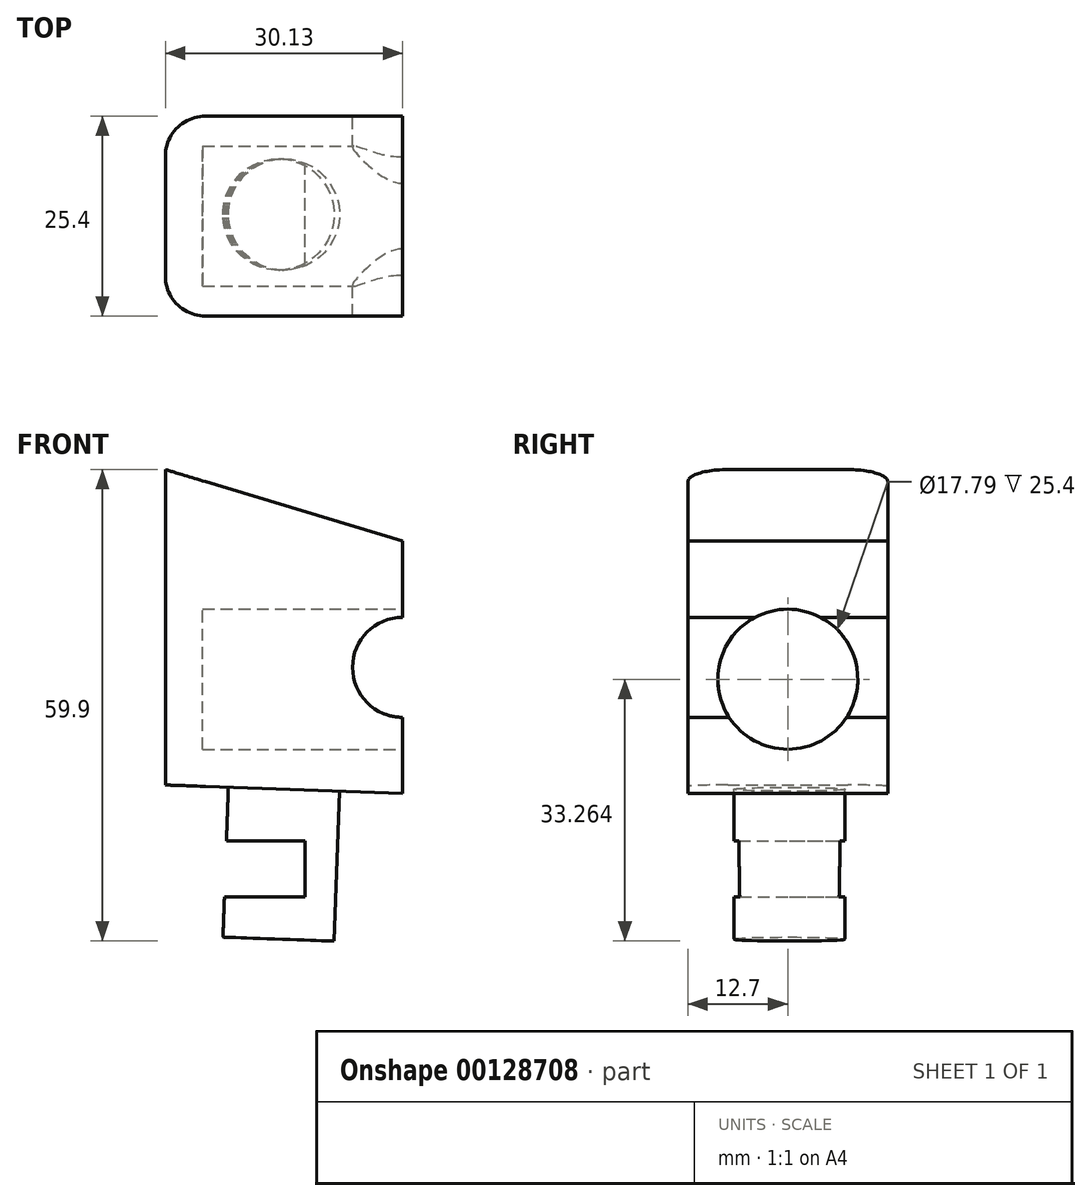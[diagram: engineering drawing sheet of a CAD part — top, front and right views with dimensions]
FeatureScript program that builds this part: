
annotation { "Feature Type Name" : "Feature", "Feature Type Description" : "" }
export const myFeature = defineFeature(function(context is Context, id is Id, definition is map)
    precondition{}
    {
        {
            var Q0;
            Q0=qCreatedBy(makeId("Front.planeOp"),FACE);
            var sketch = newSketch(context, id + "F0", { "sketchPlane" : qUnion([Q0])});
            skLineSegment(sketch, "E0", {"start": v(-39, 50.96) * mm, "end": v(-8.87, 41.86) * mm});
            skLineSegment(sketch, "E1", {"start": v(-8.87, 41.86) * mm, "end": v(-8.87, 9.8) * mm});
            skLineSegment(sketch, "E2", {"start": v(-39, 50.96) * mm, "end": v(-39, 10.89) * mm});
            skLineSegment(sketch, "E3", {"start": v(-39, 10.89) * mm, "end": v(-8.87, 9.8) * mm});
            skSolve(sketch);
        }
        {
            var Q0;
            Q0 = qSketchRegion(id + "F0", true);
            extrude(context, id + "F1", {"entities" : qUnion([Q0]), "depth" : 25.4 * mm});
        }
        {
            var Q0;
            Q0=makeQuery(id+"F1.opExtrude","SWEPT_FACE",FACE,{"disambiguationData":[OSD([sQuery(id+"F0.wireOp",EDGE,"E1")])]});
            var sketch = newSketch(context, id + "F2", { "sketchPlane" : qUnion([Q0])});
            skCircle(sketch, "E4", {"center": v(-12.7, 24.32) * mm, "radius": 8.9 * mm});
            skPoint(sketch, "E4.centerSnap0", {"position": v(-12.7, 41.86) * mm});
            skSolve(sketch);
        }
        {
            var Q0;
            Q0 = qSketchRegion(id + "F2", true);
            extrude(context, id + "F3", {"entities" : qUnion([Q0]), "operationType" : NewBodyOperationType.ADD, "oppositeDirection" : true, "depth" : 12.7 * mm});
        }
        {
            var Q0;
            Q0 = qSketchRegion(id + "F2", true);
            extrude(context, id + "F4", {"entities" : qUnion([Q0]), "operationType" : NewBodyOperationType.REMOVE, "oppositeDirection" : true, "depth" : 25.4 * mm});
        }
        {
            var Q0;
            Q0=makeQuery(id+"F1.opExtrude","SWEPT_FACE",FACE,{"disambiguationData":[OSD([sQuery(id+"F0.wireOp",EDGE,"E3")])]});
            var sketch = newSketch(context, id + "F5", { "sketchPlane" : qUnion([Q0])});
            skCircle(sketch, "E5", {"center": v(-24.3, 12.5) * mm, "radius": 7.07 * mm});
            skPoint(sketch, "E5.centerSnap0", {"position": v(-24.3, 25.4) * mm});
            skSolve(sketch);
        }
        {
            var Q0;
            Q0 = qSketchRegion(id + "F5", true);
            extrude(context, id + "F6", {"entities" : qUnion([Q0]), "operationType" : NewBodyOperationType.ADD, "depth" : 19.05 * mm});
        }
        {
            var Q0;
            Q0=qCreatedBy(makeId("Front.planeOp"),FACE);
            var sketch = newSketch(context, id + "F7", { "sketchPlane" : qUnion([Q0])});
            skLineSegment(sketch, "E6.bottom", {"start": v(-21.26, 3.8) * mm, "end": v(-34.42, 3.8) * mm});
            skLineSegment(sketch, "E6.top", {"start": v(-21.26, -3.34) * mm, "end": v(-34.42, -3.34) * mm});
            skLineSegment(sketch, "E6.left", {"start": v(-21.26, 3.8) * mm, "end": v(-21.26, -3.34) * mm});
            skLineSegment(sketch, "E6.right", {"start": v(-34.42, 3.8) * mm, "end": v(-34.42, -3.34) * mm});
            skSolve(sketch);
        }
        {
            var Q0;
            Q0 = qSketchRegion(id + "F7", true);
            extrude(context, id + "F8", {"entities" : qUnion([Q0]), "operationType" : NewBodyOperationType.REMOVE, "endBound" : BoundingType.THROUGH_ALL, "depth" : 25.4 * mm});
        }
        {
            var Q0;
            Q0=makeQuery(id+"F1.opExtrude","CAP_FACE",FACE,{"disambiguationData":[OSD([sQuery(id+"F0.wireOp",EDGE,"E0"),sQuery(id+"F0.wireOp",EDGE,"E1"),sQuery(id+"F0.wireOp",EDGE,"E2"),sQuery(id+"F0.wireOp",EDGE,"E3")])],"isStart":true});
            var sketch = newSketch(context, id + "F9", { "sketchPlane" : qUnion([Q0])});
            skCircle(sketch, "E7", {"center": v(8.87, 25.84) * mm, "radius": 6.35 * mm});
            skSolve(sketch);
        }
        {
            var Q0;
            Q0 = qSketchRegion(id + "F9", true);
            extrude(context, id + "F10", {"entities" : qUnion([Q0]), "operationType" : NewBodyOperationType.REMOVE, "endBound" : BoundingType.THROUGH_ALL, "oppositeDirection" : true, "depth" : 25.4 * mm});
        }
        {
            var Q0;
            Q0=makeQuery(id+"F1.opExtrude","CAP_EDGE",EDGE,{"disambiguationData":[OSD([sQuery(id+"F0.wireOp",EDGE,"E2")])],"isStart":true});
            fillet(context, id + "F11", {"entities" : qUnion([Q0]), "radius" : 5.08 * mm, "tangentPropagation" : true, "allowEdgeOverflow" : false});
        }
        {
            var Q0;
            Q0=makeQuery(id+"F1.opExtrude","CAP_EDGE",EDGE,{"disambiguationData":[OSD([sQuery(id+"F0.wireOp",EDGE,"E2")])],"isStart":false});
            fillet(context, id + "F12", {"entities" : qUnion([Q0]), "radius" : 5.08 * mm, "tangentPropagation" : true, "allowEdgeOverflow" : false});
        }
    });
